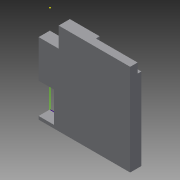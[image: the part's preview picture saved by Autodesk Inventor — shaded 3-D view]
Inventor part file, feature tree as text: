
AUTODESK INVENTOR PART (.ipt)
format: ipt  version: 2015 (Build 190159000, 159)  size: 179,200 bytes
history: native  units: mm
features: sketch x4, extrude x3
ambient origin geometry x8: Origin, YZ Plane, XZ Plane, XY Plane, X Axis, Y Axis, Z Axis, Center Point
bodies: Solid1 (feature_tree)
feature tree (7):
  extrude  "Extrusion1"  Depth=25.0mm
  extrude  "Extrusion2"  Depth=12.5mm
  extrude  "Extrusion3"  Depth=6.0mm
  sketch  "Sketch4"  dims[d8=26.0mm d9=26.0mm d10=6.0mm d11=12.0mm d12=19.1mm d13=19.1mm d14=9.55mm d15=19.1mm d16=19.1mm d17=9.55mm d22=0.0mm d23=0.0mm d24=2.0mm d25=2.0mm d26=114.3mm d28=57.15mm d29=57.15mm d30=114.3mm d37=28.575mm d38=28.575mm d39=6.4mm d40=6.4mm d41=6.4mm d43=120.0deg d44=120.0deg d45=32.127187mm d46=28.575mm d47=28.575mm d48=28.575mm d49=28.575mm d50=28.575mm d51=28.575mm d52=6.4mm d53=6.4mm d54=6.4mm d55=120.0deg d56=120.0deg d57=32.127187mm d58=6.4mm d59=6.4mm d60=6.4mm d61=120.0deg d62=120.0deg d63=32.127187mm d64=6.4mm d65=6.4mm d66=6.4mm d67=120.0deg d68=120.0deg d69=32.127187mm d70=7.0mm d71=0.0mm d72=2.0mm d73=0.0mm d74=4.65mm d75=0.0mm]
  sketch  "Sketch1"  dims[d2=25.0mm d3=25.0mm]
  sketch  "Sketch2"  dims[d4=12.5mm d5=12.5mm]
  sketch  "Sketch3"  dims[d6=6.0mm d7=12.0mm]
